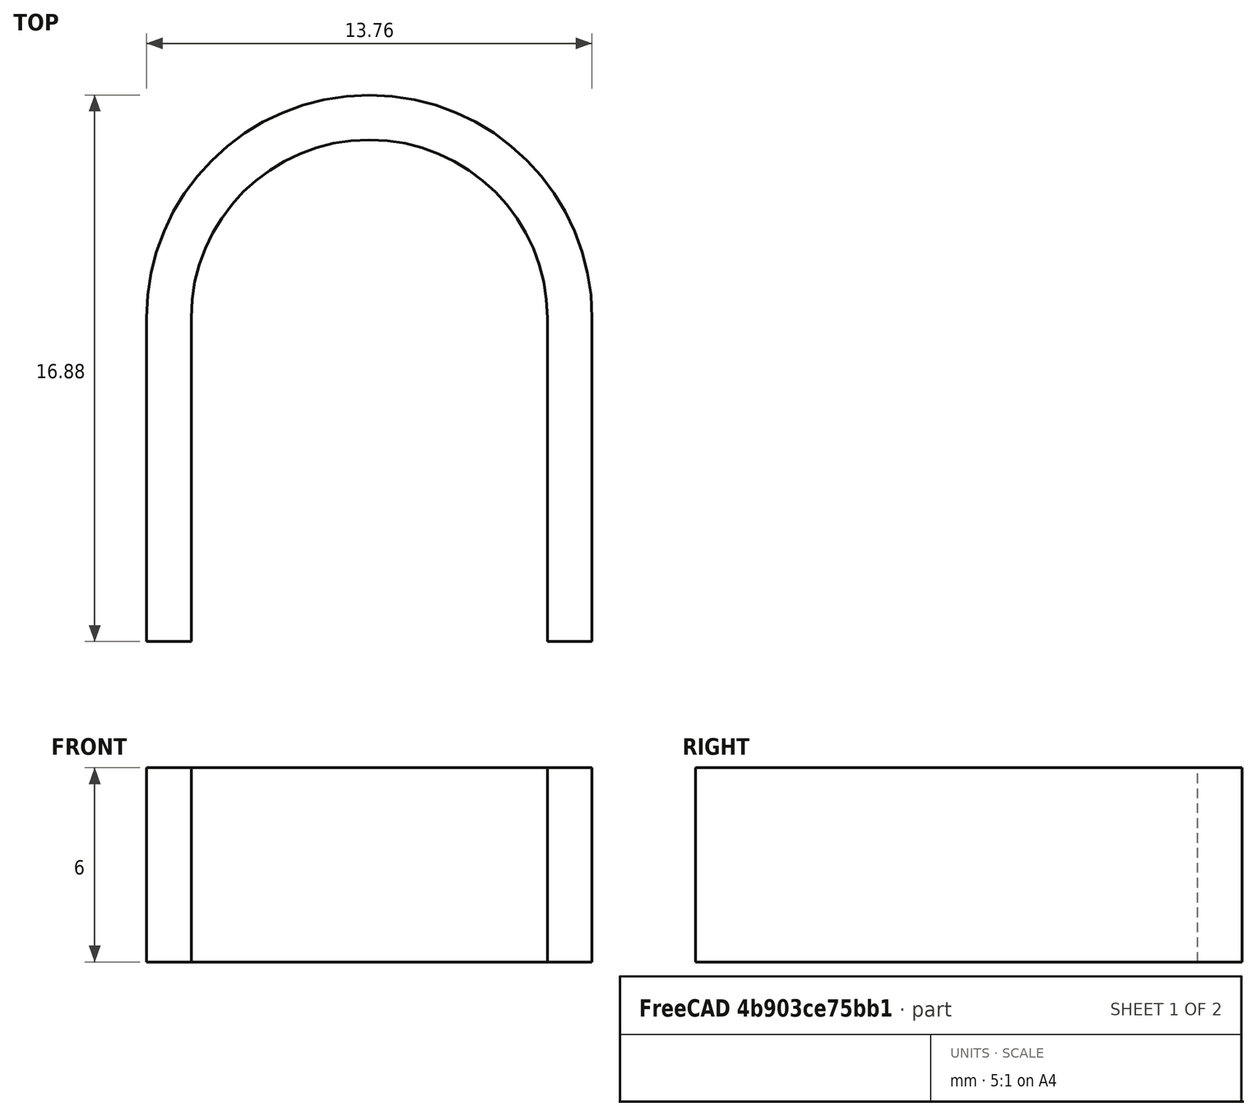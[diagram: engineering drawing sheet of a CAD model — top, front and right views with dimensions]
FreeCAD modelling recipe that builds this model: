
FCSTD DOCUMENT  (FreeCAD 0.20R27078 (Git))
Label: belt 20 toothed idler 180 deg
License: All rights reserved
LicenseURL: http://en.wikipedia.org/wiki/All_rights_reserved
objects: Sketcher::SketchObject×2, PartDesign::AdditivePipe×1, PartDesign::Body×1
note: 5 computed .brp shape members not serialized (recipe doc carries the construction recipe); baked Part::Feature solids carry a one-line shape summary decoded from their .brp

FEATURE [Sketcher::SketchObject] Sketch013
  FullyConstrained = true
  MapMode = 5
  Placement = pos=(0,0,0) rot=(1,0,0;1.5708rad)
  Support = -> [XZ_Plane009]
  sketch-geometry (4):
    g0: LineSegment StartX=0 StartY=6 StartZ=0 EndX=1.38 EndY=6 EndZ=0
    g1: LineSegment StartX=1.38 StartY=6 StartZ=0 EndX=1.38 EndY=0 EndZ=0
    g2: LineSegment StartX=1.38 StartY=0 StartZ=0 EndX=0 EndY=0 EndZ=0
    g3: LineSegment StartX=0 StartY=0 StartZ=0 EndX=0 EndY=6 EndZ=0
  constraints (12):
    c: Coincident(g0,g1)
    c: Coincident(g1,g2)
    c: Coincident(g2,g3)
    c: Coincident(g3,g0)
    c: Horizontal(g0)
    c: Horizontal(g2)
    c: Vertical(g1)
    c: Vertical(g3)
    c: PointOnObject(g0,g-2)
    c: PointOnObject(g1,g-1)
    c: DistanceY(g3,g3) = 6
    c: DistanceX(g0,g0) = 1.38
FEATURE [Sketcher::SketchObject] Sketch014
  ExternalGeometry = -> [Sketch013]
  FullyConstrained = true
  MapMode = 5
  Support = -> [XY_Plane009]
  sketch-geometry (3):
    g0: ArcOfCircle CenterX=6.88 CenterY=0 CenterZ=0 NormalX=0 NormalY=0 NormalZ=1 AngleXU=0 Radius=5.5 StartAngle=2e-16 EndAngle=3.14159
    g1: LineSegment StartX=1.38 StartY=0 StartZ=0 EndX=1.38 EndY=-10 EndZ=0
    g2: LineSegment StartX=12.38 StartY=7e-16 StartZ=0 EndX=12.38 EndY=-10 EndZ=0
  constraints (10):
    c: Coincident(g0,g-3)
    c: Horizontal(g0,g0)
    c: Radius(g0) = 5.5
    c: PointOnObject(g0,g-1)
    c: Coincident(g1,g0)
    c: Vertical(g1)
    c: Coincident(g2,g0)
    c: Vertical(g2)
    c: DistanceY(g1,g1) = 10
    c: Equal(g2,g1)
FEATURE [PartDesign::AdditivePipe] AdditivePipe004
  AuxilleryCurvelinear = true
  AuxillerySpineTangent = false
  Binormal = (0,0,0)
  Mode = 0
  Placement = pos=(0,0,0) rot=(1,0,0;1.5708rad)
  Profile = -> Sketch013
  Spine = -> Sketch014
  SpineTangent = false
  Transformation = 0
  Transition = 0
FEATURE [PartDesign::Body] Body009  label="belt 20 toothed idler 180 deg"
  Group = -> [Sketch013,Sketch014,AdditivePipe004]
  Origin = -> Origin009
  Tip = -> AdditivePipe004
